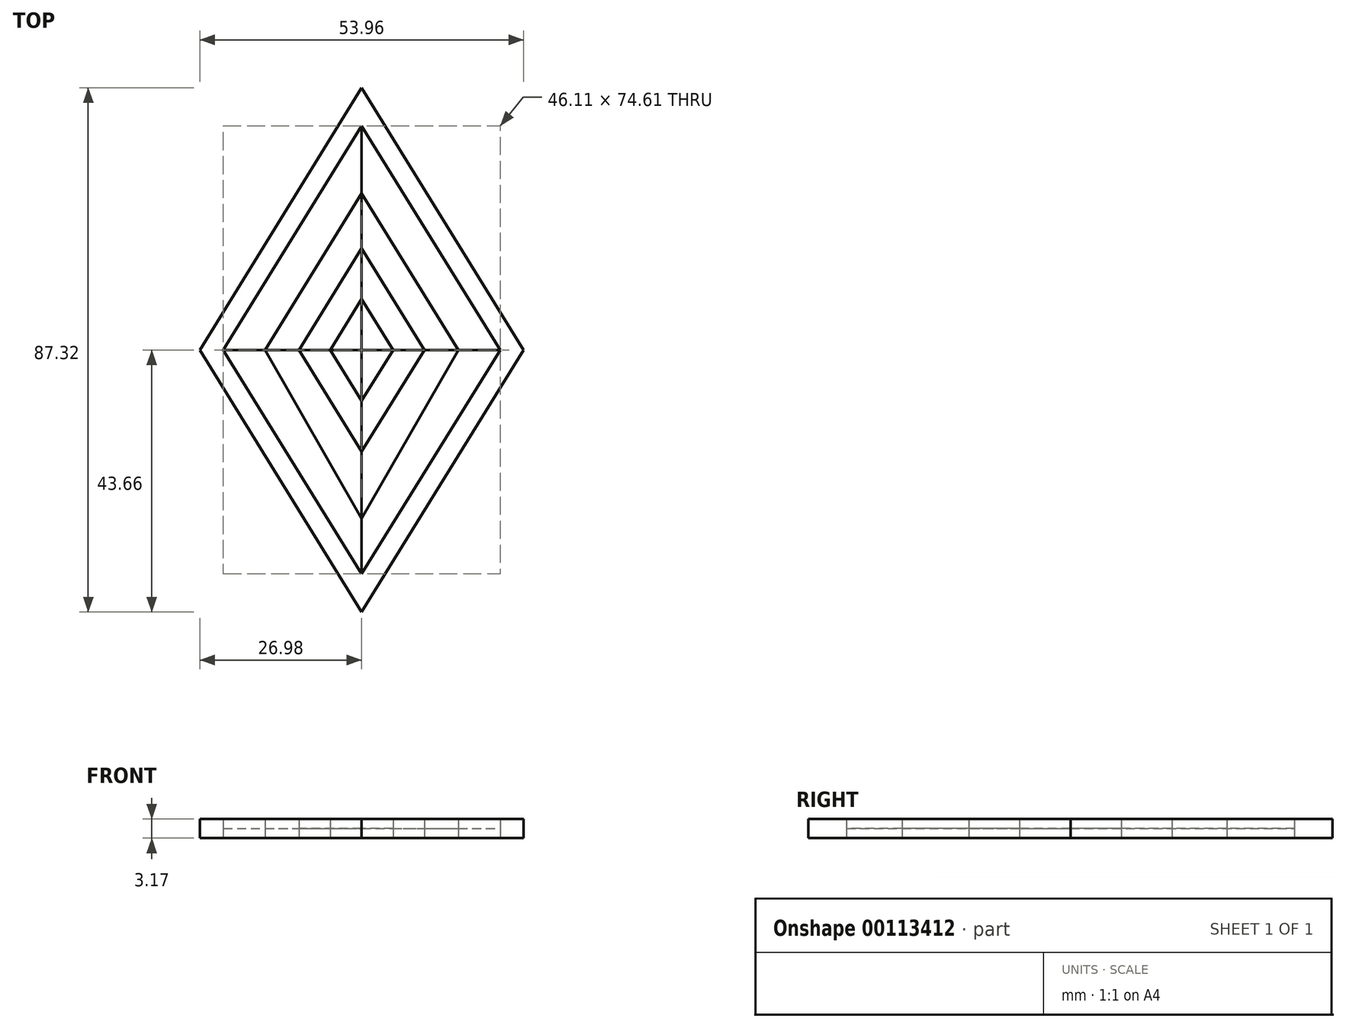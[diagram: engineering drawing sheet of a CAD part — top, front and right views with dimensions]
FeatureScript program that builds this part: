
annotation { "Feature Type Name" : "Feature", "Feature Type Description" : "" }
export const myFeature = defineFeature(function(context is Context, id is Id, definition is map)
    precondition{}
    {
        {
            var Q0;
            Q0=qCreatedBy(makeId("Top.planeOp"),FACE);
            var sketch = newSketch(context, id + "F0", { "sketchPlane" : qUnion([Q0])});
            skLineSegment(sketch, "E0", {"start": v(-68.24, 43.66) * mm, "end": v(-95.22, 0) * mm});
            skLineSegment(sketch, "E1", {"start": v(-95.22, 0) * mm, "end": v(-68.24, -43.66) * mm});
            skLineSegment(sketch, "E2", {"start": v(-68.24, -43.66) * mm, "end": v(-41.26, 0) * mm});
            skLineSegment(sketch, "E3", {"start": v(-41.26, 0) * mm, "end": v(-68.24, 43.66) * mm});
            skLineSegment(sketch, "E4", {"start": v(-68.24, -43.66) * mm, "end": v(-68.24, -37.3) * mm, "construction": true});
            skLineSegment(sketch, "E5", {"start": v(-68.24, 43.66) * mm, "end": v(-68.24, 37.3) * mm, "construction": true});
            skLineSegment(sketch, "E6", {"start": v(-95.22, 0) * mm, "end": v(-91.3, 0) * mm, "construction": true});
            skLineSegment(sketch, "E7", {"start": v(-41.26, 0) * mm, "end": v(-45.18, 0) * mm, "construction": true});
            skLineSegment(sketch, "E8", {"start": v(-45.18, 0) * mm, "end": v(-68.24, 37.3) * mm});
            skLineSegment(sketch, "E9", {"start": v(-91.3, 0) * mm, "end": v(-68.24, 37.3) * mm});
            skLineSegment(sketch, "E10", {"start": v(-91.3, 0) * mm, "end": v(-68.24, -37.3) * mm});
            skLineSegment(sketch, "E11", {"start": v(-68.24, -37.3) * mm, "end": v(-45.18, 0) * mm});
            skLineSegment(sketch, "E12", {"start": v(-68.24, 37.3) * mm, "end": v(-68.24, -37.3) * mm, "construction": true});
            skLineSegment(sketch, "E13", {"start": v(-91.3, 0) * mm, "end": v(-45.18, 0) * mm});
            skLineSegment(sketch, "E14", {"start": v(-68.24, 37.3) * mm, "end": v(-68.24, -37.3) * mm});
            skLineSegment(sketch, "E15", {"start": v(-78.7, 0) * mm, "end": v(-68.24, 16.92) * mm});
            skLineSegment(sketch, "E16", {"start": v(-68.24, 16.92) * mm, "end": v(-57.78, 0) * mm});
            skLineSegment(sketch, "E17", {"start": v(-57.78, 0) * mm, "end": v(-68.24, -16.92) * mm});
            skLineSegment(sketch, "E18", {"start": v(-68.24, -16.92) * mm, "end": v(-78.7, 0) * mm});
            skLineSegment(sketch, "E19", {"start": v(-68.24, 26.04) * mm, "end": v(-84.34, 0) * mm});
            skLineSegment(sketch, "E20", {"start": v(-84.34, 0) * mm, "end": v(-68.24, -28.08) * mm});
            skLineSegment(sketch, "E21", {"start": v(-68.24, -28.08) * mm, "end": v(-52.14, 0) * mm});
            skLineSegment(sketch, "E22", {"start": v(-52.14, 0) * mm, "end": v(-68.24, 26.04) * mm});
            skLineSegment(sketch, "E23", {"start": v(-68.24, -8.46) * mm, "end": v(-73.47, 0) * mm});
            skLineSegment(sketch, "E24", {"start": v(-73.47, 0) * mm, "end": v(-68.24, 8.46) * mm});
            skLineSegment(sketch, "E25", {"start": v(-68.24, 8.46) * mm, "end": v(-63.01, 0) * mm});
            skLineSegment(sketch, "E26", {"start": v(-63.01, 0) * mm, "end": v(-68.24, -8.46) * mm});
            skSolve(sketch);
        }
        {
            var Q0;
            Q0=makeQuery(id+"F0.imprint","IMPRINT",FACE,{"disambiguationData":[TD([[makeQuery(id+"F0.imprint","IMPRINT",EDGE,{"derivedFrom":sQuery(id+"F0.wireOp",EDGE,"E0")}),1.0]])]});
            extrude(context, id + "F1", {"entities" : qUnion([Q0]), "depth" : 3.17 * mm});
        }
        {
            var Q0;
            {var subQ0=sQuery(id+"F0.wireOp",EDGE,"E16");Q0=makeQuery(id+"F0.imprint","IMPRINT",FACE,{"disambiguationData":[TD([[makeQuery(id+"F0.imprint","IMPRINT",EDGE,{"derivedFrom":subQ0}),1.0]])]});}
            var Q1;
            {var subQ0=sQuery(id+"F0.wireOp",EDGE,"E25");Q1=makeQuery(id+"F0.imprint","IMPRINT",FACE,{"disambiguationData":[TD([[makeQuery(id+"F0.imprint","IMPRINT",EDGE,{"derivedFrom":subQ0}),-1.0]])]});}
            var Q2;
            {var subQ0=sQuery(id+"F0.wireOp",EDGE,"E15");Q2=makeQuery(id+"F0.imprint","IMPRINT",FACE,{"disambiguationData":[TD([[makeQuery(id+"F0.imprint","IMPRINT",EDGE,{"derivedFrom":subQ0}),-1.0]])]});}
            var Q3;
            {var subQ0=sQuery(id+"F0.wireOp",EDGE,"E9");Q3=makeQuery(id+"F0.imprint","IMPRINT",FACE,{"disambiguationData":[TD([[makeQuery(id+"F0.imprint","IMPRINT",EDGE,{"derivedFrom":subQ0}),-1.0]])]});}
            var Q4;
            {var subQ0=sQuery(id+"F0.wireOp",EDGE,"E18");Q4=makeQuery(id+"F0.imprint","IMPRINT",FACE,{"disambiguationData":[TD([[makeQuery(id+"F0.imprint","IMPRINT",EDGE,{"derivedFrom":subQ0}),1.0]])]});}
            var Q5;
            {var subQ0=sQuery(id+"F0.wireOp",EDGE,"E23");Q5=makeQuery(id+"F0.imprint","IMPRINT",FACE,{"disambiguationData":[TD([[makeQuery(id+"F0.imprint","IMPRINT",EDGE,{"derivedFrom":subQ0}),-1.0]])]});}
            var Q6;
            {var subQ0=sQuery(id+"F0.wireOp",EDGE,"E17");Q6=makeQuery(id+"F0.imprint","IMPRINT",FACE,{"disambiguationData":[TD([[makeQuery(id+"F0.imprint","IMPRINT",EDGE,{"derivedFrom":subQ0}),-1.0]])]});}
            var Q7;
            {var subQ0=sQuery(id+"F0.wireOp",EDGE,"E11");Q7=makeQuery(id+"F0.imprint","IMPRINT",FACE,{"disambiguationData":[TD([[makeQuery(id+"F0.imprint","IMPRINT",EDGE,{"derivedFrom":subQ0}),1.0]])]});}
            extrude(context, id + "F2", {"entities" : qUnion([Q0, Q1, Q2, Q3, Q4, Q5, Q6, Q7]), "operationType" : NewBodyOperationType.ADD, "depth" : 1.59 * mm});
        }
        {
            var Q0;
            {var subQ0=sQuery(id+"F0.wireOp",EDGE,"E8");Q0=makeQuery(id+"F0.imprint","IMPRINT",FACE,{"disambiguationData":[TD([[makeQuery(id+"F0.imprint","IMPRINT",EDGE,{"derivedFrom":subQ0}),1.0]])]});}
            var Q1;
            {var subQ0=sQuery(id+"F0.wireOp",EDGE,"E16");Q1=makeQuery(id+"F0.imprint","IMPRINT",FACE,{"disambiguationData":[TD([[makeQuery(id+"F0.imprint","IMPRINT",EDGE,{"derivedFrom":subQ0}),-1.0]])]});}
            var Q2;
            {var subQ0=sQuery(id+"F0.wireOp",EDGE,"E24");Q2=makeQuery(id+"F0.imprint","IMPRINT",FACE,{"disambiguationData":[TD([[makeQuery(id+"F0.imprint","IMPRINT",EDGE,{"derivedFrom":subQ0}),-1.0]])]});}
            var Q3;
            {var subQ0=sQuery(id+"F0.wireOp",EDGE,"E15");Q3=makeQuery(id+"F0.imprint","IMPRINT",FACE,{"disambiguationData":[TD([[makeQuery(id+"F0.imprint","IMPRINT",EDGE,{"derivedFrom":subQ0}),1.0]])]});}
            var Q4;
            {var subQ0=sQuery(id+"F0.wireOp",EDGE,"E10");Q4=makeQuery(id+"F0.imprint","IMPRINT",FACE,{"disambiguationData":[TD([[makeQuery(id+"F0.imprint","IMPRINT",EDGE,{"derivedFrom":subQ0}),1.0]])]});}
            var Q5;
            {var subQ0=sQuery(id+"F0.wireOp",EDGE,"E18");Q5=makeQuery(id+"F0.imprint","IMPRINT",FACE,{"disambiguationData":[TD([[makeQuery(id+"F0.imprint","IMPRINT",EDGE,{"derivedFrom":subQ0}),-1.0]])]});}
            var Q6;
            {var subQ0=sQuery(id+"F0.wireOp",EDGE,"E26");Q6=makeQuery(id+"F0.imprint","IMPRINT",FACE,{"disambiguationData":[TD([[makeQuery(id+"F0.imprint","IMPRINT",EDGE,{"derivedFrom":subQ0}),-1.0]])]});}
            var Q7;
            {var subQ0=sQuery(id+"F0.wireOp",EDGE,"E17");Q7=makeQuery(id+"F0.imprint","IMPRINT",FACE,{"disambiguationData":[TD([[makeQuery(id+"F0.imprint","IMPRINT",EDGE,{"derivedFrom":subQ0}),1.0]])]});}
            extrude(context, id + "F3", {"entities" : qUnion([Q0, Q1, Q2, Q3, Q4, Q5, Q6, Q7]), "depth" : 3.17 * mm});
        }
    });
